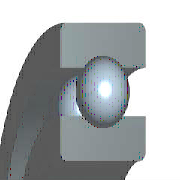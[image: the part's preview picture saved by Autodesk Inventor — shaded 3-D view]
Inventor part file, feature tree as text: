
AUTODESK INVENTOR PART (.ipt)
format: ipt  version: 2022 (Build 260153000, 153)  size: 347,136 bytes
history: native  units: mm (DEFAULTED — no unit token found)
features: other x3, plane x2, sketch x1
ambient origin geometry x8: Origin, YZ Plane, XZ Plane, XY Plane, X Axis, Y Axis, Z Axis, Center Point
bodies: Solid1 (feature_tree)
feature tree (6):
  other  "WorkPoint1"
  other  "WorkAxis1"
  plane  "WorkPlane3"
  plane  "WorkPlane4"
  other  "WorkPoint2"
  sketch  "Эскиз5"
